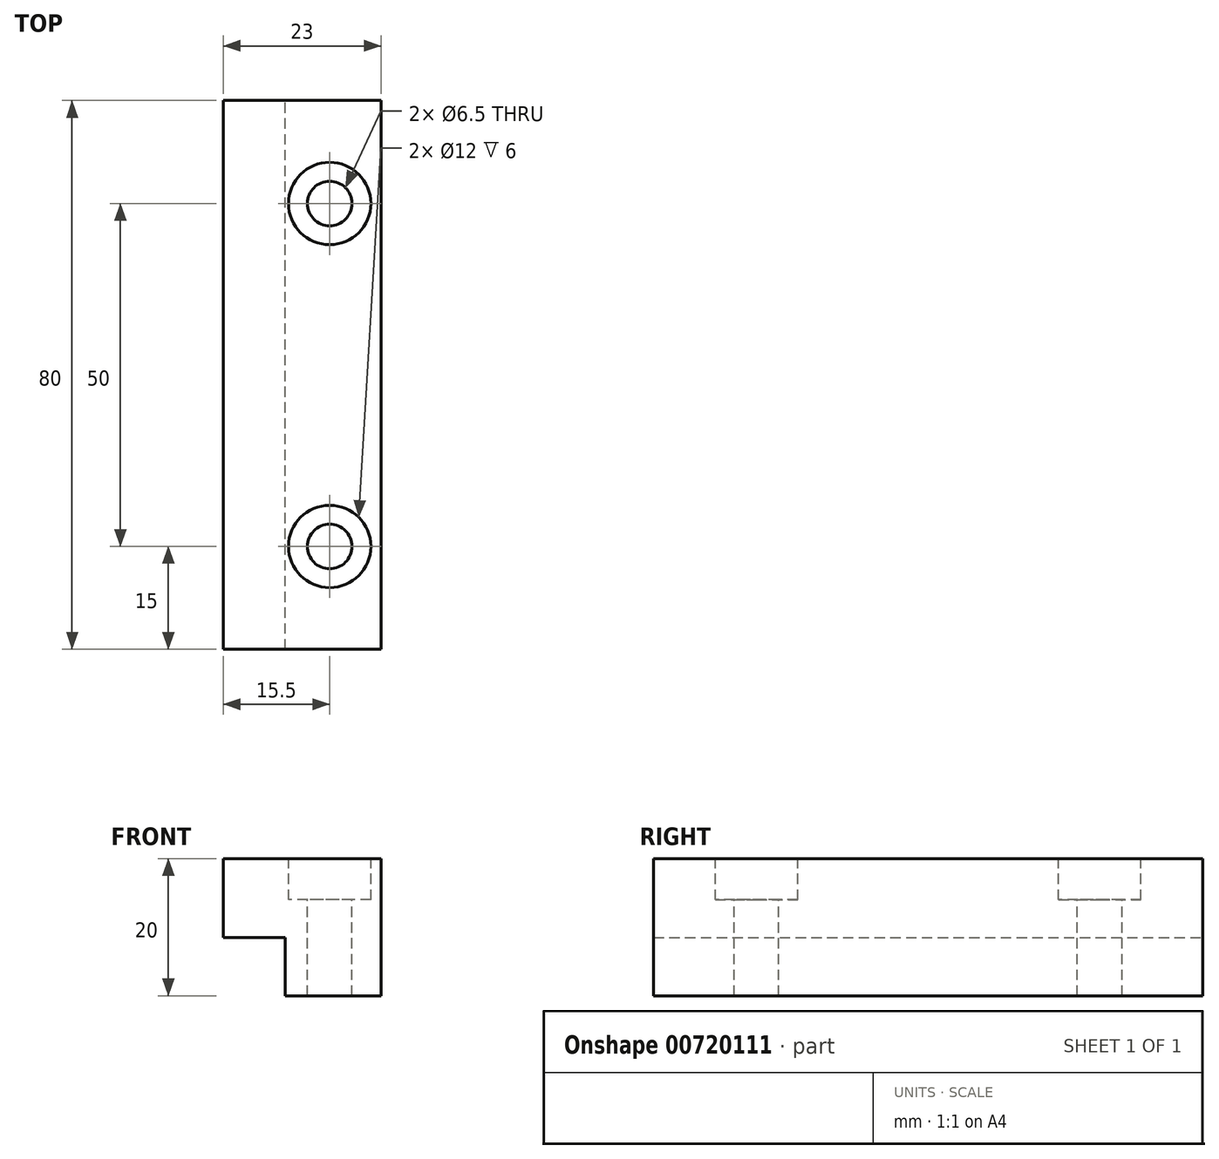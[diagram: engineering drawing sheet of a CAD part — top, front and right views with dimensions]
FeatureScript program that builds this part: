
annotation { "Feature Type Name" : "Feature", "Feature Type Description" : "" }
export const myFeature = defineFeature(function(context is Context, id is Id, definition is map)
    precondition{}
    {
        {
            var Q0;
            Q0=qCreatedBy(makeId("Front.planeOp"),FACE);
            var sketch = newSketch(context, id + "F0", { "sketchPlane" : qUnion([Q0])});
            skLineSegment(sketch, "E0", {"start": v(0, 0) * mm, "end": v(0, 20) * mm});
            skLineSegment(sketch, "E1", {"start": v(0, 20) * mm, "end": v(-23, 20) * mm});
            skLineSegment(sketch, "E2", {"start": v(-23, 20) * mm, "end": v(-23, 8.5) * mm});
            skLineSegment(sketch, "E3", {"start": v(-23, 8.5) * mm, "end": v(-14, 8.5) * mm});
            skLineSegment(sketch, "E4", {"start": v(-14, 8.5) * mm, "end": v(-14, 0) * mm});
            skLineSegment(sketch, "E5", {"start": v(-14, 0) * mm, "end": v(0, 0) * mm});
            skSolve(sketch);
        }
        {
            var Q0;
            Q0=makeQuery(id+"F0.imprint","IMPRINT",FACE,{"disambiguationData":[TD([[makeQuery(id+"F0.imprint","IMPRINT",EDGE,{"derivedFrom":sQuery(id+"F0.wireOp",EDGE,"E0")}),1.0]])]});
            extrude(context, id + "F1", {"entities" : qUnion([Q0]), "depth" : 80 * mm, "offsetDistance" : 25 * mm});
        }
        {
            var Q0;
            Q0=makeQuery(id+"F1.opExtrude","SWEPT_FACE",FACE,{"disambiguationData":[OSD([sQuery(id+"F0.wireOp",EDGE,"E1")])]});
            var sketch = newSketch(context, id + "F2", { "sketchPlane" : qUnion([Q0])});
            skCircle(sketch, "E6", {"center": v(-7.5, -15) * mm, "radius": 3.25 * mm});
            skCircle(sketch, "E7", {"center": v(-7.5, -65) * mm, "radius": 3.25 * mm});
            skSolve(sketch);
        }
        {
            var Q0;
            Q0=makeQuery(id+"F2.imprint","IMPRINT",FACE,{"disambiguationData":[TD([[makeQuery(id+"F2.imprint","IMPRINT",EDGE,{"derivedFrom":sQuery(id+"F2.wireOp",EDGE,"E6")}),1.0]])]});
            var Q1;
            Q1=makeQuery(id+"F2.imprint","IMPRINT",FACE,{"disambiguationData":[TD([[makeQuery(id+"F2.imprint","IMPRINT",EDGE,{"derivedFrom":sQuery(id+"F2.wireOp",EDGE,"E7")}),1.0]])]});
            extrude(context, id + "F3", {"entities" : qUnion([Q0, Q1]), "operationType" : NewBodyOperationType.REMOVE, "endBound" : BoundingType.THROUGH_ALL, "oppositeDirection" : true, "depth" : 25 * mm, "offsetDistance" : 25 * mm});
        }
        {
            var Q0;
            Q0=makeQuery(id+"F1.opExtrude","SWEPT_FACE",FACE,{"disambiguationData":[OSD([sQuery(id+"F0.wireOp",EDGE,"E1")])]});
            var sketch = newSketch(context, id + "F4", { "sketchPlane" : qUnion([Q0])});
            skCircle(sketch, "E8", {"center": v(-7.5, -15) * mm, "radius": 6 * mm});
            skCircle(sketch, "E9", {"center": v(-7.5, -65) * mm, "radius": 6 * mm});
            skSolve(sketch);
        }
        {
            var Q0;
            Q0=makeQuery(id+"F4.imprint","IMPRINT",FACE,{"disambiguationData":[TD([[makeQuery(id+"F4.imprint","IMPRINT",EDGE,{"derivedFrom":sQuery(id+"F4.wireOp",EDGE,"E8")}),1.0]])]});
            var Q1;
            Q1=makeQuery(id+"F4.imprint","IMPRINT",FACE,{"disambiguationData":[TD([[makeQuery(id+"F4.imprint","IMPRINT",EDGE,{"derivedFrom":sQuery(id+"F4.wireOp",EDGE,"E9")}),1.0]])]});
            extrude(context, id + "F5", {"entities" : qUnion([Q0, Q1]), "operationType" : NewBodyOperationType.REMOVE, "oppositeDirection" : true, "depth" : 6 * mm, "offsetDistance" : 25 * mm});
        }
    });
